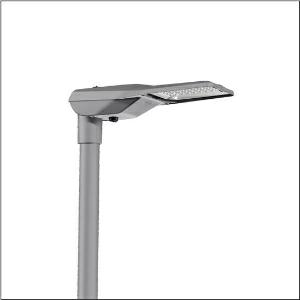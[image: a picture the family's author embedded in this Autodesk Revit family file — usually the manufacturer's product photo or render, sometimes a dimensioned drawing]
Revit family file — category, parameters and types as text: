
# Revit family: streetlight_sl_21_iq_mini___st0_5a_5xe2b31y08jb_a8c8
name_source: partatom
category: Lighting Fixtures
units: mm (PartAtom-declared; Revit-internal decimal feet)

## family parameters
Cut with Voids When Loaded = No
Host = Face
Light Source = No
Part Type = Normal
Room Calculation Point = No
Round Connector Dimension = Use Diameter
Shared = No

## types (1)
- --- (1 x LED, 11210 lm, 72.5 W, 3000K)
    Apparent Load = 73 VA
    CIE Flux Codes = 43 76 97 100 100
    Color Rendering = 70
    Color Temperature = 3000K
    Default Elevation = 1800 mm
    Description = Streetlight SL 21 iQ mini, mast luminaire, primary light control with lens, of PMMA, primary optical cover: cover, of toughened safety glass, transparent, light distribution: ST0.5a, light emission: direct distribution, primary light characteristic: asymmetric, installation type: post-top, side-entry, LED, High Power LED, rated luminous flux: 11.210lm, luminous efficacy: 155lm/W, light colour: 730, colour temperature: 3000K, control: presetting dimming logarithmic, Street-Remote, Auto-Match, Temp-Guard, Lumen-Switch, Night-Set, Smart-Wire, Light-Fading, Desk-Remote (wireless, voltage-free reading and setting of iQ features in the workshop via application-optimized NFC function/RFID function), optimised constant luminous flux control (CLO 2.0), mains connection: 220..240V, AC, 50/60Hz, start of lifetime: 73W, end of service life: 76W, reduction: 33W, luminaire housing, of diecast aluminium, powder-coated, Siteco® metallic grey (DB 702S), corrosivity category C5 mid according to DIN EN ISO 12944, please order mast flange separately, inclination adjustable: 0°, 5°, 10°, 15°, sealing non-destructively replaceable, multi-level sealing system, length: 628mm, width: 235mm, height: 110mm, mast flange for spigot size: 42mm (side-entry): 5XC10008XM4, 60/48mm (side-entry/post-top): 5XC10108XM2, 76/60mm (side-entry/post-top): 5XC10108XM1, Smart Interface below and above, protection rating (complete): IP66, insulation class (complete): insulation class II (safety insulation), certification: CE, ENEC, ENEC+, VDE, impact resistance: IK09, permissible operating ambient temperature for outdoor applications: -40..+50°C, standard-compliant lighting for roads and squares, packaging unit: 1 piece

Light Distribution: ST0.5a
    Height = 110 mm
    Lamp = 1 x LED
    Lamp Light Flux = 11210 lm
    Lamp Power = 72.5 W
    Lamp count = 1
    Length = 625 mm
    Luminous efficacy = 155 lm/W
    Manufacturer = Siteco
    ModVariant = No
    Model = 5XE2B31Y08JB
    Number of Poles = 1
    OnlyDefault = Yes
    Power Factor = 1
    Product Name = Streetlight SL 21 iQ mini | ST0.5a
    Product group = mast luminaire | pylon top
    ProductGroupID = 6100
    Protection Class = Protection class II
    Protection Degree = IP 66
    RLX_Detail_Level = 1
    RLX_Emergency_Light_Flux = 0 lm
    RLX_Emergency_Type = 0
    RLX_Emergency_Type_DB = No
    RlxData = <blob elided: 103601 chars, md5=6baa4f30>
    Socket = socket
    Standby Power = 0 W
    System Light Flux = 11210 lm
    System Power = 73 W
    Type Comments = factory setting: luminous flux: 100 % | dim-lin: 254 | 755 mA
    Type Image = l_1003514.jpg
    URL = http://relux.com
    VarID = @adj_064033
    Voltage = 0 V
    Weight = 0.00 kg
    Width = 234 mm

## geometry (parser evidence)
native form markers: Blend x4, Sweep x9
no freeform markers — native parametric forms only
